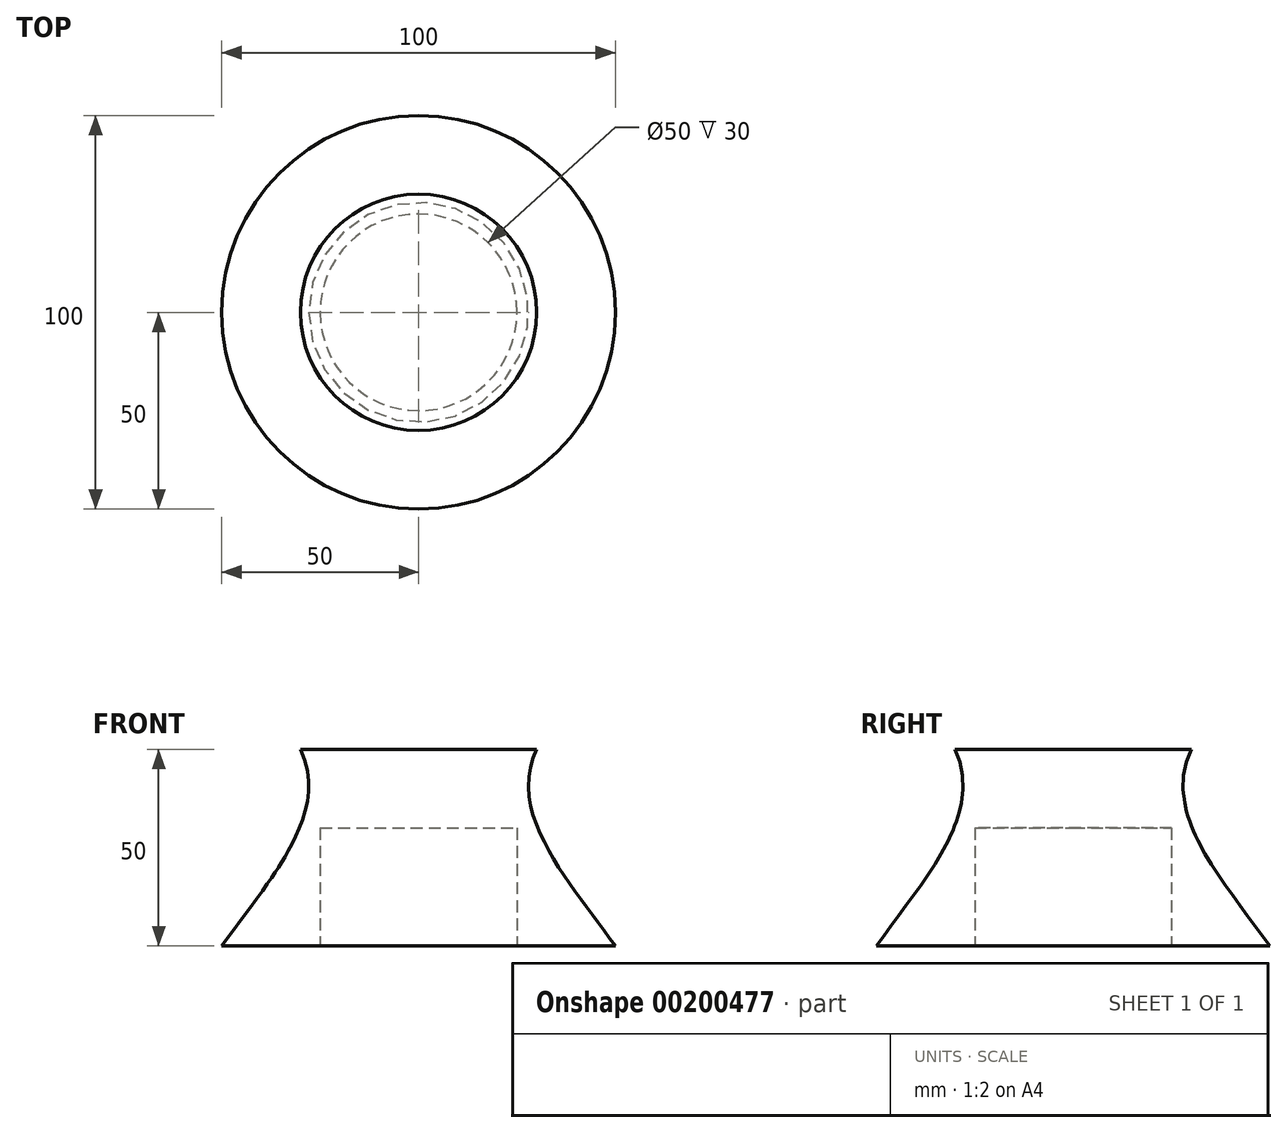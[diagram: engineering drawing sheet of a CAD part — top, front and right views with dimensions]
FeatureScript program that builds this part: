
annotation { "Feature Type Name" : "Feature", "Feature Type Description" : "" }
export const myFeature = defineFeature(function(context is Context, id is Id, definition is map)
    precondition{}
    {
        {
            var Q0;
            Q0=qCreatedBy(makeId("Front.planeOp"),FACE);
            var sketch = newSketch(context, id + "F0", { "sketchPlane" : qUnion([Q0])});
            skLineSegment(sketch, "E0", {"start": v(0, 0) * mm, "end": v(0, 50) * mm});
            skLineSegment(sketch, "E1", {"start": v(-50, 0) * mm, "end": v(0, 0) * mm});
            skLineSegment(sketch, "E2", {"start": v(0, 50) * mm, "end": v(-30, 50) * mm});
            skFitSpline(sketch, "E3", {"points": [v(-30, 50) * mm, v(-33.3, 23.86) * mm, v(-50, 0) * mm], "startDerivative": vector(30.47, -63.73) * mm, "endDerivative": vector(-68.43, -93) * mm});
            skSolve(sketch);
        }
        {
            var Q0;
            Q0=makeQuery(id+"F0.imprint","IMPRINT",FACE,{"disambiguationData":[TD([[makeQuery(id+"F0.imprint","IMPRINT",EDGE,{"derivedFrom":sQuery(id+"F0.wireOp",EDGE,"E0")}),1.0]])]});
            var Q1;
            Q1=sQuery(id+"F0.wireOp",EDGE,"E0");
            revolve(context, id + "F1", {"entities" : qUnion([Q0]), "axis" : qUnion([Q1]), "revolveType" : RevolveType.FULL});
        }
        {
            var Q0;
            Q0=makeQuery(id+"F1.opRevolve","SWEPT_FACE",FACE,{"disambiguationData":[OSD([sQuery(id+"F0.wireOp",EDGE,"E1")])]});
            var sketch = newSketch(context, id + "F2", { "sketchPlane" : qUnion([Q0])});
            skCircle(sketch, "E4", {"center": v(0, 0) * mm, "radius": 25 * mm});
            skSolve(sketch);
        }
        {
            var Q0;
            Q0 = qSketchRegion(id + "F2", true);
            extrude(context, id + "F3", {"entities" : qUnion([Q0]), "operationType" : NewBodyOperationType.REMOVE, "oppositeDirection" : true, "depth" : 30 * mm});
        }
    });
